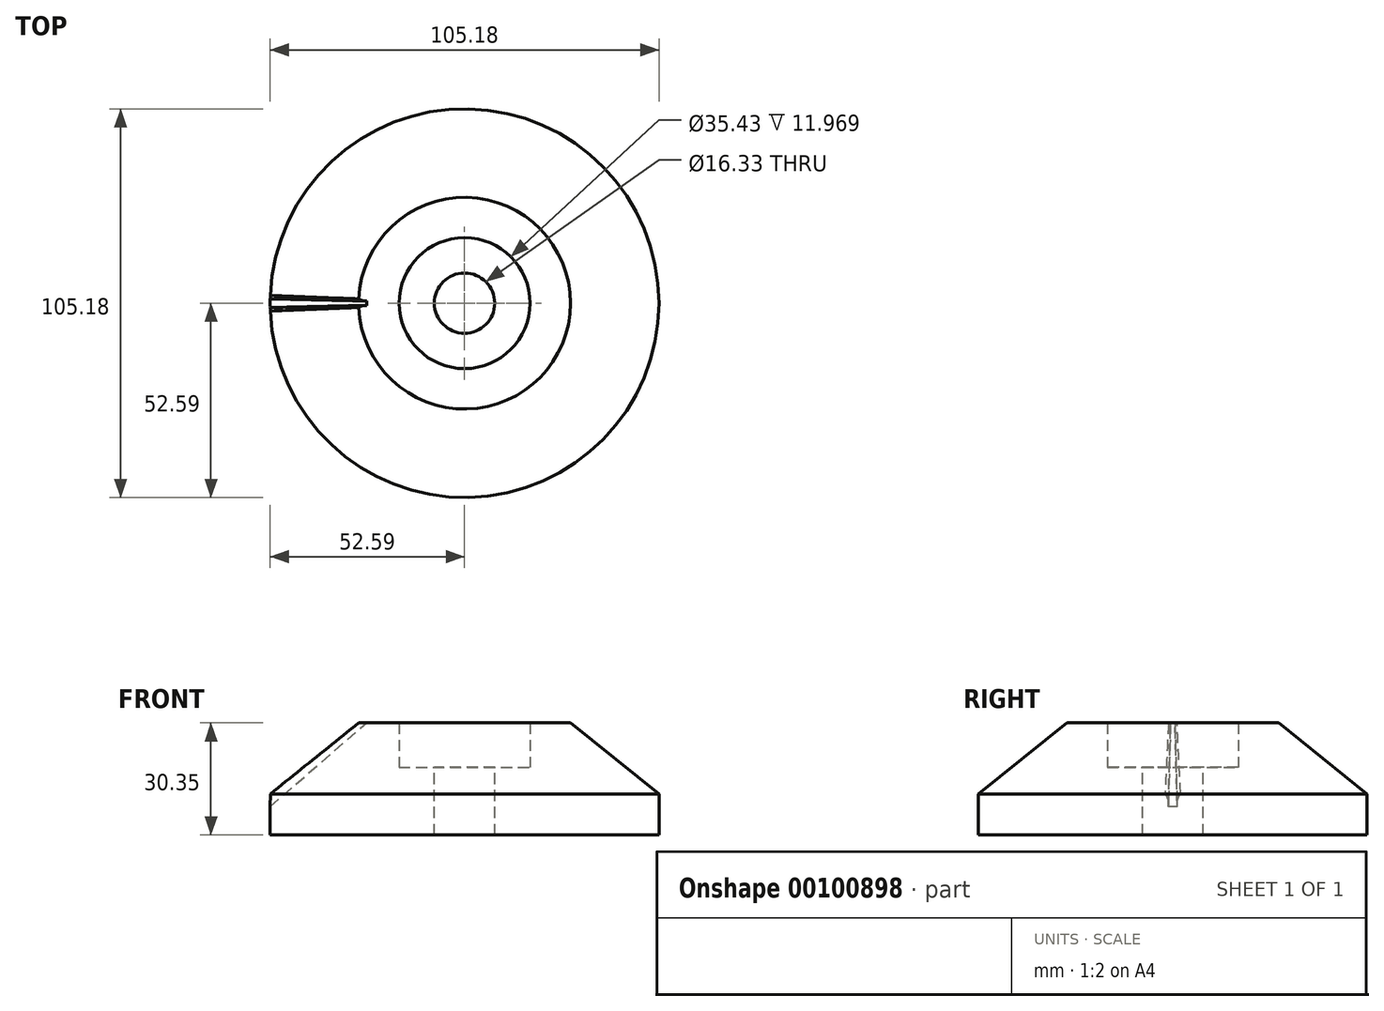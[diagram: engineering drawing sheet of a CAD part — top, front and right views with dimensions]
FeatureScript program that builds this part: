
annotation { "Feature Type Name" : "Feature", "Feature Type Description" : "" }
export const myFeature = defineFeature(function(context is Context, id is Id, definition is map)
    precondition{}
    {
        {
            var Q0;
            Q0=qCreatedBy(makeId("Front.planeOp"),FACE);
            var sketch = newSketch(context, id + "F0", { "sketchPlane" : qUnion([Q0])});
            skLineSegment(sketch, "E0", {"start": v(0, 0) * mm, "end": v(-17.72, 0) * mm});
            skLineSegment(sketch, "E1", {"start": v(-17.72, 0) * mm, "end": v(-17.72, 11.97) * mm});
            skLineSegment(sketch, "E2", {"start": v(-17.72, 11.97) * mm, "end": v(-28.65, 11.97) * mm});
            skLineSegment(sketch, "E3", {"start": v(-28.65, 11.97) * mm, "end": v(-52.59, -7.26) * mm});
            skLineSegment(sketch, "E4", {"start": v(-52.59, -7.26) * mm, "end": v(-52.59, -18.38) * mm});
            skLineSegment(sketch, "E5", {"start": v(-52.59, -18.38) * mm, "end": v(0, -18.38) * mm});
            skLineSegment(sketch, "E6", {"start": v(0, -18.38) * mm, "end": v(0, 0) * mm});
            skSolve(sketch);
        }
        {
            var Q0;
            Q0 = qSketchRegion(id + "F0", true);
            var Q1;
            Q1=sQuery(id+"F0.wireOp",EDGE,"E6");
            revolve(context, id + "F1", {"entities" : qUnion([Q0]), "axis" : qUnion([Q1]), "revolveType" : RevolveType.FULL});
        }
        {
            var Q0;
            Q0=qCreatedBy(makeId("Front.planeOp"),FACE);
            var sketch = newSketch(context, id + "F2", { "sketchPlane" : qUnion([Q0])});
            skLineSegment(sketch, "E7", {"start": v(0, -18.61) * mm, "end": v(0, 90.45) * mm, "construction": true});
            skLineSegment(sketch, "E8", {"start": v(0, 34.98) * mm, "end": v(-66.43, -18.38) * mm, "construction": true});
            skLineSegment(sketch, "E9", {"start": v(28.65, 11.97) * mm, "end": v(52.59, -7.26) * mm});
            skLineSegment(sketch, "E10", {"start": v(-52.59, -7.26) * mm, "end": v(-28.65, 11.97) * mm, "construction": true});
            skPoint(sketch, "E11", {"position": v(0, 34.98) * mm});
            skSolve(sketch);
        }
        {
            var Q0;
            Q0=sQuery(id+"F2.wireOp",EDGE,"E8");
            var Q1;
            Q1=sQuery(id+"F2.wireOp",VERTEX,"E8.end");
            cPlane(context, id + "F3", {"entities" : qUnion([Q0, Q1]), "cplaneType" : CPlaneType.LINE_POINT, "offset" : 152.4 * mm, "width" : 152.4 * mm, "height" : 152.4 * mm});
        }
        {
            var Q0;
            Q0=qCreatedBy(id+"F3.planeOp",FACE);
            var sketch = newSketch(context, id + "F4", { "sketchPlane" : qUnion([Q0])});
            skLineSegment(sketch, "E12", {"start": v(0, 24) * mm, "end": v(-1.48, 24) * mm});
            skLineSegment(sketch, "E13", {"start": v(0, 28.2) * mm, "end": v(-5.16, 28.2) * mm});
            skArc(sketch, "E14", {"start": v(-1.48, 24) * mm, "mid": v(-2.37, 26.93) * mm, "end": v(-5.16, 28.2) * mm});
            skLineSegment(sketch, "E15.MirrorCS", {"start": v(0, 28.2) * mm, "end": v(5.16, 28.2) * mm});
            skArc(sketch, "E16.MirrorCS", {"start": v(1.48, 24) * mm, "mid": v(2.37, 26.93) * mm, "end": v(5.16, 28.2) * mm});
            skLineSegment(sketch, "E17.MirrorCS", {"start": v(0, 24) * mm, "end": v(1.48, 24) * mm});
            skSolve(sketch);
        }
        {
            var Q1;
            Q1=makeQuery(id+"F4.imprint","IMPRINT",FACE,{"disambiguationData":[TD([[makeQuery(id+"F4.imprint","IMPRINT",EDGE,{"derivedFrom":sQuery(id+"F4.wireOp",EDGE,"E12")}),-1.0]])]});
            var Q2;
            Q2=sQuery(id+"F2.wireOp",VERTEX,"E11");
            loft(context, id + "F5", {"operationType" : NewBodyOperationType.REMOVE, "sheetProfilesArray" : [{ "sheetProfileEntities" : qUnion([Q1]) }, { "sheetProfileEntities" : qUnion([Q2]) }]});
        }
        {
            var Q0;
            Q0=makeQuery(id+"F1.opRevolve","SWEPT_FACE",FACE,{"disambiguationData":[OSD([sQuery(id+"F0.wireOp",EDGE,"E0")])]});
            var sketch = newSketch(context, id + "F6", { "sketchPlane" : qUnion([Q0])});
            skCircle(sketch, "E18", {"center": v(0, 0) * mm, "radius": 8.16 * mm});
            skSolve(sketch);
        }
        {
            var Q0;
            Q0 = qSketchRegion(id + "F6", true);
            var Q1;
            Q1=makeQuery(id+"F1.opRevolve","SWEPT_FACE",FACE,{"disambiguationData":[OSD([sQuery(id+"F0.wireOp",EDGE,"E5")])]});
            extrude(context, id + "F7", {"entities" : qUnion([Q0]), "operationType" : NewBodyOperationType.REMOVE, "endBound" : BoundingType.UP_TO_SURFACE, "oppositeDirection" : true, "endBoundEntityFace" : qUnion([Q1]), "depth" : 25.4 * mm});
        }
    });
